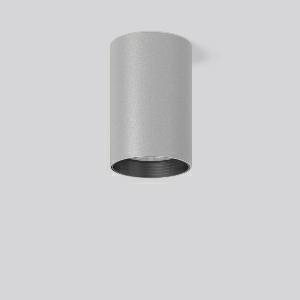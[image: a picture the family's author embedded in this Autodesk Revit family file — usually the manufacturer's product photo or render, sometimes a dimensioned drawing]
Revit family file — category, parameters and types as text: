
# Revit family: heledon_maxi_a_931236_004_76_fbef
name_source: partatom
category: Lighting Fixtures
units: mm (PartAtom-declared; Revit-internal decimal feet)

## family parameters
Cut with Voids When Loaded = No
Host = Face
Light Source = No
Part Type = Normal
Room Calculation Point = No
Round Connector Dimension = Use Diameter
Shared = No

## types (1)
- HELEDON maxi A (1 x LED Modul 932 fresh meat, 1800 lm, 3200)
    Apparent Load = 33 VA
    Approval mark = CE
    CIE Flux Codes = 96 99 100 100 100
    Color Rendering = 90
    Color Temperature = 3200
    Default Elevation = 1800 mm  [stored 5.90551 ft]
    Description = Series: HELEDON maxi
Cylindrical surface-mounted downlight. Housing: die-cast aluminium, powder-coated. Internal ceiling frame polycarbonate with bayonet mounting. Black plastic ring and recessed LED to prevent glare from the side. Optical assembly with lens made of plastic (polycarbonate) for the best homogeneous light distribution - can be changed without tools. Special LED for illumination of meat included. Suitable for Ceiling mounting. Easy installation with a separate ceiling frame with bayonet mounting and plug connection. Driver integrated. Connected via plug-in connector. High quality converter without flickering and stroboscopic effect. The following accessories can be mounted without use of tools: interchangeable lenses, decorative glasses, honeycomb louvre, clear and frosted diffusers, white interchangeable plastic ring. 
Colour: silver
Diameter: 123 mm
Height: 183 mm
Lamp: LED
Socket: without socket
Colour temperature: fresh meat
System power: 33 W
Rated luminous flux: 1800 lm
Luminous efficiency: 55 lm/W
Control gear: Converter, dimmable, DALI
Protection class: I
Type of protection: IP 20
    Height = 183 mm
    Lamp = 1 x LED Modul 932 fresh meat
    Lamp Light Flux = 1800 lm
    Lamp count = 1
    Length = 123 mm
    Lifetime = 50000 h
    Luminous efficacy = 55 lm/W
    Manufacturer = RZB
    ModVariant = No
    Model = 931236.004.76
    Mounting Place = Ceiling
    Mounting Type = Surface mounted
    Number of Poles = 1
    OnlyDefault = Yes
    Power Factor = 1
    Product Name = HELEDON maxi A
    Product group = Surface mounted downlights
    ProductGroupID = 302
    Protection Class = Protection class I
    Protection Degree = IP 20
    RLX_Detail_Level = 1
    RLX_Emergency_Light_Flux = 0 lm
    RLX_Emergency_Type = 0
    RLX_Emergency_Type_DB = No
    RlxData = <blob elided: 98257 chars, md5=47b65ce9>
    Socket = socket
    Standby Power = 0 W
    System Light Flux = 1800 lm
    System Power = 33 W
    Type Comments = Product without accessories
    Type Image = 931193.004.jpg
    URL = http://relux.com
    VarID = ---
    Voltage = 230 V
    Voltage Range = 220-240 V
    Weight = 0.00 kg
    Width = 0 mm  [stored 0 ft]

note: [stored X ft] marks values corroborated as IEEE doubles in the binary element streams (Revit-internal decimal feet)

## geometry (parser evidence)
native form markers: Blend x4, Sweep x11
no freeform markers — native parametric forms only
